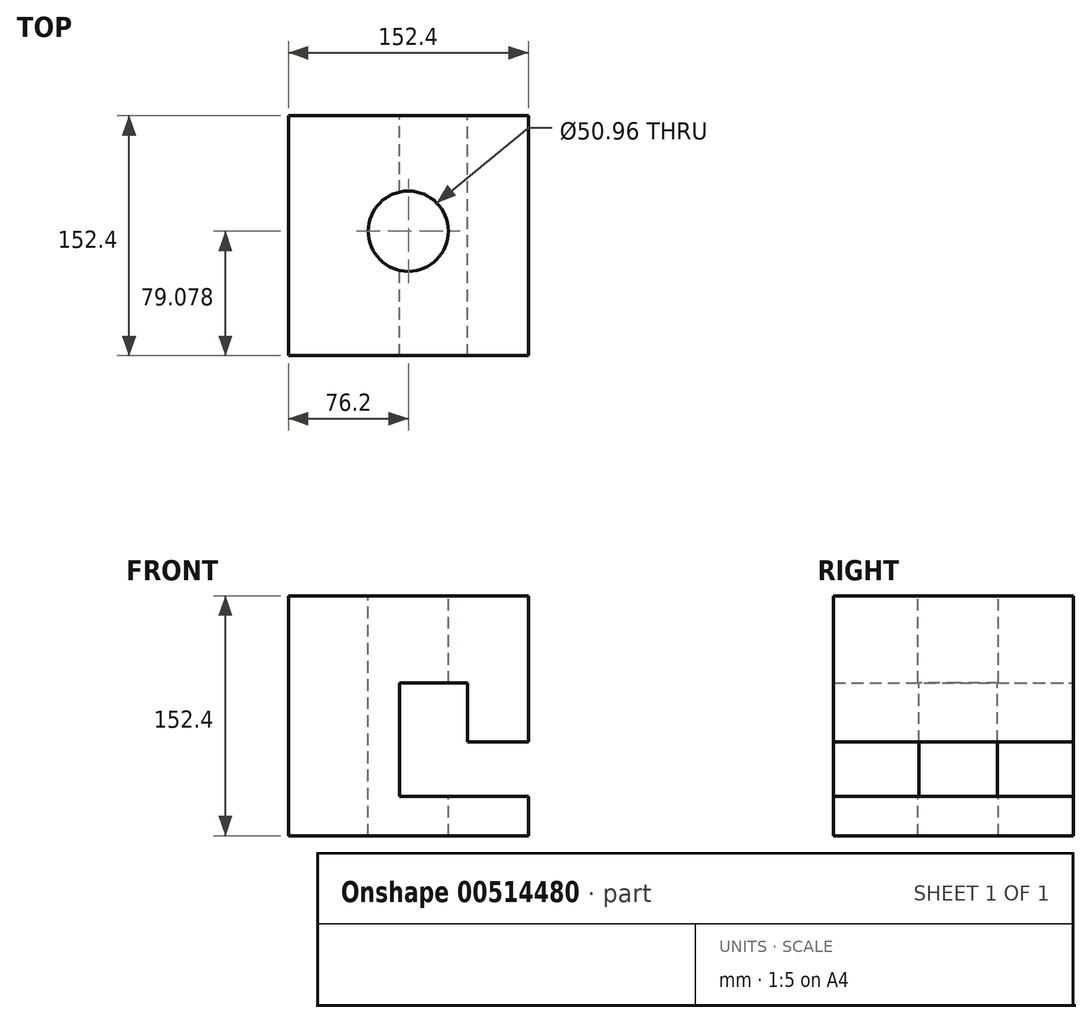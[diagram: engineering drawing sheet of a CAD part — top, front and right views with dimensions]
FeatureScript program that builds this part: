
annotation { "Feature Type Name" : "Feature", "Feature Type Description" : "" }
export const myFeature = defineFeature(function(context is Context, id is Id, definition is map)
    precondition{}
    {
        {
            var Q0;
            Q0=qCreatedBy(makeId("Top.planeOp"),FACE);
            var sketch = newSketch(context, id + "F0", { "sketchPlane" : qUnion([Q0])});
            skLineSegment(sketch, "E0.bottom", {"start": v(-76.2, 76.2) * mm, "end": v(76.2, 76.2) * mm});
            skLineSegment(sketch, "E0.top", {"start": v(-76.2, -76.2) * mm, "end": v(76.2, -76.2) * mm});
            skLineSegment(sketch, "E0.left", {"start": v(-76.2, 76.2) * mm, "end": v(-76.2, -76.2) * mm});
            skLineSegment(sketch, "E0.right", {"start": v(76.2, 76.2) * mm, "end": v(76.2, -76.2) * mm});
            skPoint(sketch, "E0.middle", {"position": v(0, 0) * mm});
            skSolve(sketch);
        }
        {
            var Q0;
            Q0=makeQuery(id+"F0.imprint","IMPRINT",FACE,{"disambiguationData":[TD([[makeQuery(id+"F0.imprint","IMPRINT",EDGE,{"derivedFrom":sQuery(id+"F0.wireOp",EDGE,"E0.bottom")}),-1.0]])]});
            extrude(context, id + "F1", {"entities" : qUnion([Q0]), "depth" : 152.4 * mm});
        }
        {
            var Q0;
            Q0=makeQuery(id+"F1.opExtrude","CAP_FACE",FACE,{"disambiguationData":[OSD([sQuery(id+"F0.wireOp",EDGE,"E0.bottom"),sQuery(id+"F0.wireOp",EDGE,"E0.top"),sQuery(id+"F0.wireOp",EDGE,"E0.left"),sQuery(id+"F0.wireOp",EDGE,"E0.right")])],"isStart":false});
            var sketch = newSketch(context, id + "F2", { "sketchPlane" : qUnion([Q0])});
            skCircle(sketch, "E1", {"center": v(0, 2.88) * mm, "radius": 25.48 * mm});
            skSolve(sketch);
        }
        {
            var Q0;
            Q0=makeQuery(id+"F2.imprint","IMPRINT",FACE,{"disambiguationData":[TD([[makeQuery(id+"F2.imprint","IMPRINT",EDGE,{"derivedFrom":sQuery(id+"F2.wireOp",EDGE,"E1")}),1.0]])]});
            extrude(context, id + "F3", {"entities" : qUnion([Q0]), "operationType" : NewBodyOperationType.REMOVE, "oppositeDirection" : true, "depth" : 152.4 * mm});
        }
        {
            var Q0;
            Q0=makeQuery(id+"F1.opExtrude","SWEPT_FACE",FACE,{"disambiguationData":[OSD([sQuery(id+"F0.wireOp",EDGE,"E0.bottom")])]});
            var sketch = newSketch(context, id + "F4", { "sketchPlane" : qUnion([Q0])});
            skLineSegment(sketch, "E2.bottom", {"start": v(-37.66, 97.04) * mm, "end": v(5.56, 97.04) * mm});
            skLineSegment(sketch, "E2.top", {"start": v(-37.66, 59.46) * mm, "end": v(5.56, 59.46) * mm});
            skLineSegment(sketch, "E2.left", {"start": v(-37.66, 97.04) * mm, "end": v(-37.66, 59.46) * mm});
            skLineSegment(sketch, "E2.right", {"start": v(5.56, 97.04) * mm, "end": v(5.56, 59.46) * mm});
            skLineSegment(sketch, "E3.bottom", {"start": v(5.56, 59.46) * mm, "end": v(-76.2, 59.46) * mm});
            skLineSegment(sketch, "E3.top", {"start": v(5.56, 24.86) * mm, "end": v(-76.2, 24.86) * mm});
            skLineSegment(sketch, "E3.left", {"start": v(5.56, 59.46) * mm, "end": v(5.56, 24.86) * mm});
            skLineSegment(sketch, "E3.right", {"start": v(-76.2, 59.46) * mm, "end": v(-76.2, 24.86) * mm});
            skSolve(sketch);
        }
        {
            var Q0;
            Q0 = qSketchRegion(id + "F4", true);
            extrude(context, id + "F5", {"entities" : qUnion([Q0]), "operationType" : NewBodyOperationType.REMOVE, "oppositeDirection" : true, "depth" : 152.4 * mm});
        }
    });
